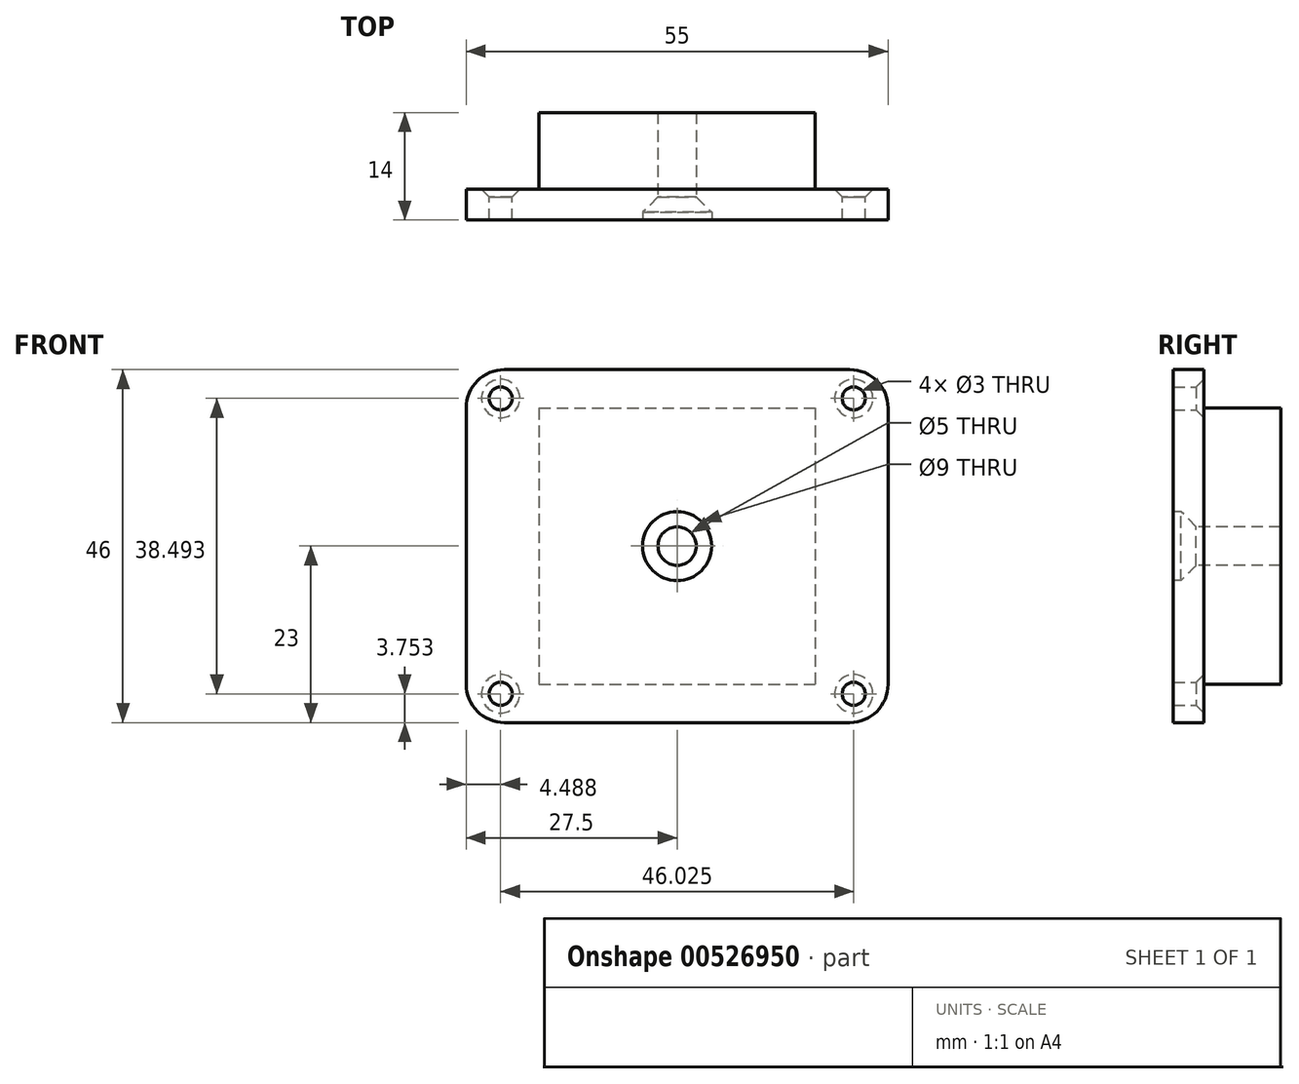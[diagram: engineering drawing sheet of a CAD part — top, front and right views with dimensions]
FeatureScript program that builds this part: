
annotation { "Feature Type Name" : "Feature", "Feature Type Description" : "" }
export const myFeature = defineFeature(function(context is Context, id is Id, definition is map)
    precondition{}
    {
        {
            var Q0;
            Q0=qCreatedBy(makeId("Front.planeOp"),FACE);
            var sketch = newSketch(context, id + "F0", { "sketchPlane" : qUnion([Q0])});
            skLineSegment(sketch, "E0.bottom", {"start": v(-18, 18) * mm, "end": v(18, 18) * mm});
            skLineSegment(sketch, "E0.top", {"start": v(-18, -18) * mm, "end": v(18, -18) * mm});
            skLineSegment(sketch, "E0.left", {"start": v(-18, 18) * mm, "end": v(-18, -18) * mm});
            skLineSegment(sketch, "E0.right", {"start": v(18, 18) * mm, "end": v(18, -18) * mm});
            skPoint(sketch, "E0.middle", {"position": v(0, 0) * mm});
            skLineSegment(sketch, "E1.bottom", {"start": v(-27.5, 23) * mm, "end": v(27.5, 23) * mm});
            skLineSegment(sketch, "E1.top", {"start": v(-27.5, -23) * mm, "end": v(27.5, -23) * mm});
            skLineSegment(sketch, "E1.left", {"start": v(-27.5, 23) * mm, "end": v(-27.5, -23) * mm});
            skLineSegment(sketch, "E1.right", {"start": v(27.5, 23) * mm, "end": v(27.5, -23) * mm});
            skPoint(sketch, "E2", {"position": v(-23.01, 19.25) * mm});
            skPoint(sketch, "E3", {"position": v(23.01, 19.25) * mm});
            skPoint(sketch, "E4", {"position": v(23.01, -19.25) * mm});
            skPoint(sketch, "E5", {"position": v(-23.01, -19.25) * mm});
            skSolve(sketch);
        }
        {
            var Q0;
            Q0=makeQuery(id+"F0.imprint","IMPRINT",FACE,{"disambiguationData":[TD([[makeQuery(id+"F0.imprint","IMPRINT",EDGE,{"derivedFrom":sQuery(id+"F0.wireOp",EDGE,"E0.bottom")}),1.0]])]});
            var Q1;
            Q1=makeQuery(id+"F0.imprint","IMPRINT",FACE,{"disambiguationData":[TD([[makeQuery(id+"F0.imprint","IMPRINT",EDGE,{"derivedFrom":sQuery(id+"F0.wireOp",EDGE,"E0.bottom")}),-1.0]])]});
            extrude(context, id + "F1", {"entities" : qUnion([Q0, Q1]), "depth" : 4 * mm, "offsetDistance" : 25 * mm});
        }
        {
            var Q0;
            Q0=makeQuery(id+"F0.imprint","IMPRINT",FACE,{"disambiguationData":[TD([[makeQuery(id+"F0.imprint","IMPRINT",EDGE,{"derivedFrom":sQuery(id+"F0.wireOp",EDGE,"E0.bottom")}),-1.0]])]});
            extrude(context, id + "F2", {"entities" : qUnion([Q0]), "operationType" : NewBodyOperationType.ADD, "oppositeDirection" : true, "depth" : 10 * mm, "offsetDistance" : 25 * mm});
        }
        {
            var Q0;
            Q0=sQuery(id+"F0.wireOp",VERTEX,"E0.middle");
            var Q1;
            Q1=makeQuery(id+"F1.opExtrude","SWEPT_BODY",BODY,{"disambiguationData":[OSD([sQuery(id+"F0.wireOp",EDGE,"E1.bottom"),sQuery(id+"F0.wireOp",EDGE,"E1.top"),sQuery(id+"F0.wireOp",EDGE,"E1.left"),sQuery(id+"F0.wireOp",EDGE,"E1.right")])]});
            hole(context, id + "F3", {"style" : HoleStyle.SIMPLE, "endStyle" : HoleEndStyle.BLIND, "holeDiameter" : 5 * mm, "holeDepth" : 38 * mm, "isTappedThrough" : true, "tappedDepth" : 12 * mm, "tapClearance" : 3, "locations" : qUnion([Q0]), "scope" : qUnion([Q1])});
        }
        {
            var Q0;
            Q0=qCreatedBy(makeId("Front.planeOp"),FACE);
            cPlane(context, id + "F4", {"entities" : qUnion([Q0]), "cplaneType" : CPlaneType.OFFSET, "offset" : 4 * mm, "width" : 150 * mm, "height" : 150 * mm});
        }
        {
            var Q0;
            Q0=qCreatedBy(id+"F4.planeOp",FACE);
            var sketch = newSketch(context, id + "F5", { "sketchPlane" : qUnion([Q0])});
            skPoint(sketch, "E6", {"position": v(0, 0) * mm});
            skSolve(sketch);
        }
        {
            var Q0;
            Q0=qCreatedBy(makeId("Front.planeOp"),FACE);
            cPlane(context, id + "F6", {"entities" : qUnion([Q0]), "cplaneType" : CPlaneType.OFFSET, "offset" : 3 * mm, "width" : 150 * mm, "height" : 150 * mm});
        }
        {
            var Q0;
            Q0=qCreatedBy(id+"F6.planeOp",FACE);
            var sketch = newSketch(context, id + "F7", { "sketchPlane" : qUnion([Q0])});
            skPoint(sketch, "E7", {"position": v(0, 0) * mm});
            skSolve(sketch);
        }
        {
            var Q0;
            Q0=sQuery(id+"F5.wireOp",VERTEX,"E6");
            var Q1;
            Q1=makeQuery(id+"F1.opExtrude","SWEPT_BODY",BODY,{"disambiguationData":[OSD([sQuery(id+"F0.wireOp",EDGE,"E1.bottom"),sQuery(id+"F0.wireOp",EDGE,"E1.top"),sQuery(id+"F0.wireOp",EDGE,"E1.left"),sQuery(id+"F0.wireOp",EDGE,"E1.right")])]});
            hole(context, id + "F8", {"style" : HoleStyle.SIMPLE, "endStyle" : HoleEndStyle.BLIND, "holeDiameter" : 9 * mm, "holeDepth" : 1 * mm, "isTappedThrough" : true, "tappedDepth" : 12 * mm, "tapClearance" : 3, "locations" : qUnion([Q0]), "scope" : qUnion([Q1])});
        }
        {
            var Q0;
            Q0=sQuery(id+"F7.wireOp",VERTEX,"E7");
            var Q1;
            Q1=makeQuery(id+"F1.opExtrude","SWEPT_BODY",BODY,{"disambiguationData":[OSD([sQuery(id+"F0.wireOp",EDGE,"E1.bottom"),sQuery(id+"F0.wireOp",EDGE,"E1.top"),sQuery(id+"F0.wireOp",EDGE,"E1.left"),sQuery(id+"F0.wireOp",EDGE,"E1.right")])]});
            hole(context, id + "F9", {"style" : HoleStyle.C_SINK, "endStyle" : HoleEndStyle.BLIND, "holeDiameter" : 5 * mm, "cSinkDiameter" : 9 * mm, "cSinkAngle" : 90 * degree, "holeDepth" : 13 * mm, "isTappedThrough" : true, "tappedDepth" : 12 * mm, "tapClearance" : 3, "locations" : qUnion([Q0]), "scope" : qUnion([Q1])});
        }
        {
            var Q0;
            Q0=sQuery(id+"F0.wireOp",VERTEX,"E5");
            var Q1;
            Q1=sQuery(id+"F0.wireOp",VERTEX,"E4");
            var Q2;
            Q2=sQuery(id+"F0.wireOp",VERTEX,"E3");
            var Q3;
            Q3=sQuery(id+"F0.wireOp",VERTEX,"E2");
            var Q4;
            Q4=makeQuery(id+"F1.opExtrude","SWEPT_BODY",BODY,{"disambiguationData":[OSD([sQuery(id+"F0.wireOp",EDGE,"E1.bottom"),sQuery(id+"F0.wireOp",EDGE,"E1.top"),sQuery(id+"F0.wireOp",EDGE,"E1.left"),sQuery(id+"F0.wireOp",EDGE,"E1.right")])]});
            hole(context, id + "F10", {"style" : HoleStyle.C_SINK, "endStyle" : HoleEndStyle.BLIND, "oppositeDirection" : true, "holeDiameter" : 3 * mm, "cSinkDiameter" : 5 * mm, "cSinkAngle" : 90 * degree, "holeDepth" : 38 * mm, "isTappedThrough" : true, "tappedDepth" : 12 * mm, "tapClearance" : 3, "locations" : qUnion([Q0, Q1, Q2, Q3]), "scope" : qUnion([Q4])});
        }
        {
            var Q0;
            Q0=makeQuery(id+"F1.opExtrude","SWEPT_EDGE",EDGE,{"disambiguationData":[OSD([sQuery(id+"F0.wireOp",EDGE,"E1.bottom"),sQuery(id+"F0.wireOp",EDGE,"E1.left")])]});
            var Q1;
            Q1=makeQuery(id+"F1.opExtrude","SWEPT_EDGE",EDGE,{"disambiguationData":[OSD([sQuery(id+"F0.wireOp",EDGE,"E1.bottom"),sQuery(id+"F0.wireOp",EDGE,"E1.right")])]});
            var Q2;
            Q2=makeQuery(id+"F1.opExtrude","SWEPT_EDGE",EDGE,{"disambiguationData":[OSD([sQuery(id+"F0.wireOp",EDGE,"E1.top"),sQuery(id+"F0.wireOp",EDGE,"E1.left")])]});
            var Q3;
            Q3=makeQuery(id+"F1.opExtrude","SWEPT_EDGE",EDGE,{"disambiguationData":[OSD([sQuery(id+"F0.wireOp",EDGE,"E1.top"),sQuery(id+"F0.wireOp",EDGE,"E1.right")])]});
            fillet(context, id + "F11", {"entities" : qUnion([Q0, Q1, Q2, Q3]), "radius" : 5 * mm, "tangentPropagation" : true, "allowEdgeOverflow" : false});
        }
    });
